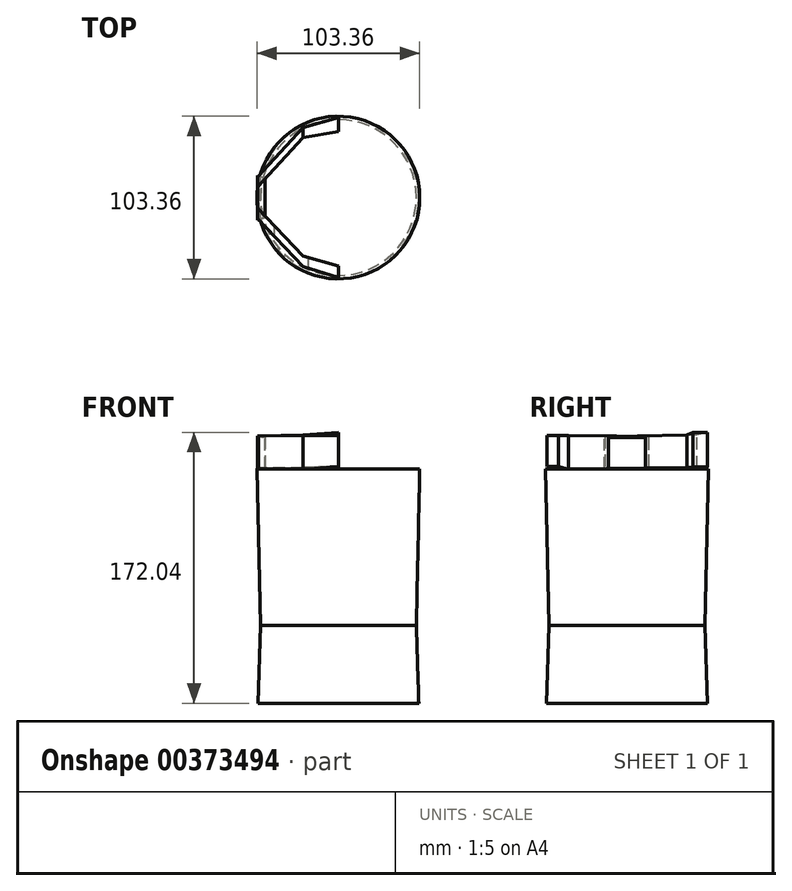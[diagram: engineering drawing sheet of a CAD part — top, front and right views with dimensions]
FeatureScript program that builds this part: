
annotation { "Feature Type Name" : "Feature", "Feature Type Description" : "" }
export const myFeature = defineFeature(function(context is Context, id is Id, definition is map)
    precondition{}
    {
        {
            var Q0;
            Q0=qCreatedBy(makeId("Top.planeOp"),FACE);
            var sketch = newSketch(context, id + "F0", { "sketchPlane" : qUnion([Q0])});
            skCircle(sketch, "E0", {"center": v(0, 0) * mm, "radius": 55.5 * mm});
            skSolve(sketch);
        }
        {
            var Q0;
            Q0=qCreatedBy(makeId("Top.planeOp"),FACE);
            cPlane(context, id + "F1", {"entities" : qUnion([Q0]), "cplaneType" : CPlaneType.OFFSET, "offset" : 25.4 * mm, "width" : 152.4 * mm, "height" : 152.4 * mm});
        }
        {
            var Q0;
            Q0=qCreatedBy(makeId("Top.planeOp"),FACE);
            cPlane(context, id + "F2", {"entities" : qUnion([Q0]), "cplaneType" : CPlaneType.OFFSET, "offset" : 25.91 * mm, "oppositeDirection" : true, "width" : 152.4 * mm, "height" : 152.4 * mm});
        }
        {
            var Q0;
            Q0=qCreatedBy(id+"F2.planeOp",FACE);
            cPlane(context, id + "F3", {"entities" : qUnion([Q0]), "cplaneType" : CPlaneType.OFFSET, "offset" : 76.15 * mm, "width" : 152.4 * mm, "height" : 152.4 * mm});
        }
        {
            var Q0;
            Q0=qCreatedBy(id+"F2.planeOp",FACE);
            cPlane(context, id + "F4", {"entities" : qUnion([Q0]), "cplaneType" : CPlaneType.OFFSET, "offset" : 23.34 * mm, "oppositeDirection" : true, "width" : 152.4 * mm, "height" : 152.4 * mm});
        }
        {
            var Q0;
            Q0=qCreatedBy(id+"F3.planeOp",FACE);
            var sketch = newSketch(context, id + "F5", { "sketchPlane" : qUnion([Q0])});
            skCircle(sketch, "E1", {"center": v(0, 0) * mm, "radius": 54.76 * mm});
            skSolve(sketch);
        }
        {
            var Q0;
            Q0=qCreatedBy(id+"F1.planeOp",FACE);
            var sketch = newSketch(context, id + "F6", { "sketchPlane" : qUnion([Q0])});
            skCircle(sketch, "E2", {"center": v(0, 0) * mm, "radius": 55.5 * mm});
            skSolve(sketch);
        }
        {
            var Q0;
            Q0=qCreatedBy(id+"F2.planeOp",FACE);
            var sketch = newSketch(context, id + "F7", { "sketchPlane" : qUnion([Q0])});
            skCircle(sketch, "E3", {"center": v(0, 0) * mm, "radius": 55.91 * mm});
            skSolve(sketch);
        }
        {
            var Q0;
            Q0=qCreatedBy(id+"F4.planeOp",FACE);
            var sketch = newSketch(context, id + "F8", { "sketchPlane" : qUnion([Q0])});
            skCircle(sketch, "E4", {"center": v(0, 0) * mm, "radius": 55.49 * mm});
            skSolve(sketch);
        }
        {
            var Q0;
            Q0=makeQuery(id+"F8.imprint","IMPRINT",FACE,{"disambiguationData":[TD([[makeQuery(id+"F8.imprint","IMPRINT",EDGE,{"derivedFrom":sQuery(id+"F8.wireOp",EDGE,"E4")}),1.0]])]});
            var sketch = newSketch(context, id + "F9", { "sketchPlane" : qUnion([Q0])});
            skCircle(sketch, "E5", {"center": v(0, 0) * mm, "radius": 49.52 * mm});
            skSolve(sketch);
        }
        {
            var Q0;
            Q0=makeQuery(id+"F5.imprint","IMPRINT",FACE,{"disambiguationData":[TD([[makeQuery(id+"F5.imprint","IMPRINT",EDGE,{"derivedFrom":sQuery(id+"F5.wireOp",EDGE,"E1")}),1.0]])]});
            var sketch = newSketch(context, id + "F10", { "sketchPlane" : qUnion([Q0])});
            skCircle(sketch, "E6", {"center": v(0, 0) * mm, "radius": 51.68 * mm});
            skSolve(sketch);
        }
        {
            var Q0;
            Q0=makeQuery(id+"F10.imprint","IMPRINT",FACE,{"disambiguationData":[TD([[makeQuery(id+"F10.imprint","IMPRINT",EDGE,{"derivedFrom":sQuery(id+"F10.wireOp",EDGE,"E6")}),1.0]])]});
            var Q1;
            Q1=makeQuery(id+"F9.imprint","IMPRINT",FACE,{"disambiguationData":[TD([[makeQuery(id+"F9.imprint","IMPRINT",EDGE,{"derivedFrom":sQuery(id+"F9.wireOp",EDGE,"E5")}),1.0]])]});
            loft(context, id + "F11", {"sheetProfilesArray" : [{ "sheetProfileEntities" : qUnion([Q0]) }, { "sheetProfileEntities" : qUnion([Q1]) }]});
        }
        {
            var Q0;
            Q0=qCreatedBy(id+"F4.planeOp",FACE);
            cPlane(context, id + "F12", {"entities" : qUnion([Q0]), "cplaneType" : CPlaneType.OFFSET, "offset" : 25.01 * mm, "oppositeDirection" : true, "width" : 152.4 * mm, "height" : 152.4 * mm});
        }
        {
            var Q0;
            Q0=qCreatedBy(id+"F12.planeOp",FACE);
            cPlane(context, id + "F13", {"entities" : qUnion([Q0]), "cplaneType" : CPlaneType.OFFSET, "offset" : 24.45 * mm, "oppositeDirection" : true, "width" : 152.4 * mm, "height" : 152.4 * mm});
        }
        {
            var Q0;
            Q0=qCreatedBy(id+"F13.planeOp",FACE);
            var sketch = newSketch(context, id + "F14", { "sketchPlane" : qUnion([Q0])});
            skCircle(sketch, "E7", {"center": v(0, 0) * mm, "radius": 51.1 * mm});
            skSolve(sketch);
        }
        {
            var Q1;
            Q1=makeQuery(id+"F14.imprint","IMPRINT",FACE,{"disambiguationData":[TD([[makeQuery(id+"F14.imprint","IMPRINT",EDGE,{"derivedFrom":sQuery(id+"F14.wireOp",EDGE,"E7")}),1.0]])]});
            var Q2;
            Q2=makeQuery(id+"F11.opLoft","CAP_FACE",FACE,{"disambiguationData":[OSD([makeQuery(id+"F9.imprint","IMPRINT",FACE,{"disambiguationData":[TD([[makeQuery(id+"F9.imprint","IMPRINT",EDGE,{"derivedFrom":sQuery(id+"F9.wireOp",EDGE,"E5")}),1.0]])]})])],"isStart":true});
            loft(context, id + "F15", {"operationType" : NewBodyOperationType.ADD, "sheetProfilesArray" : [{ "sheetProfileEntities" : qUnion([Q1]) }, { "sheetProfileEntities" : qUnion([Q2]) }]});
        }
        {
            var Q0;
            Q0=qCreatedBy(makeId("Right.planeOp"),FACE);
            cPlane(context, id + "F16", {"entities" : qUnion([Q0]), "cplaneType" : CPlaneType.OFFSET, "offset" : 51.44 * mm, "oppositeDirection" : true, "width" : 152.4 * mm, "height" : 152.4 * mm});
        }
        {
            var Q0;
            Q0=qCreatedBy(id+"F16.planeOp",FACE);
            var sketch = newSketch(context, id + "F17", { "sketchPlane" : qUnion([Q0])});
            skLineSegment(sketch, "E8.bottom", {"start": v(-14.21, 50.2) * mm, "end": v(13.86, 50.2) * mm});
            skLineSegment(sketch, "E8.top", {"start": v(-14.21, 70.79) * mm, "end": v(13.86, 70.79) * mm});
            skLineSegment(sketch, "E8.left", {"start": v(-14.21, 50.2) * mm, "end": v(-14.21, 70.79) * mm});
            skLineSegment(sketch, "E8.right", {"start": v(13.86, 50.2) * mm, "end": v(13.86, 70.79) * mm});
            skSolve(sketch);
        }
        {
            var Q0;
            Q0=qCreatedBy(id+"F16.planeOp",FACE);
            cPlane(context, id + "F18", {"entities" : qUnion([Q0]), "cplaneType" : CPlaneType.OFFSET, "offset" : 4.7 * mm, "width" : 152.4 * mm, "height" : 152.4 * mm});
        }
        {
            var Q0;
            Q0=qCreatedBy(makeId("Right.planeOp"),FACE);
            cPlane(context, id + "F19", {"entities" : qUnion([Q0]), "cplaneType" : CPlaneType.OFFSET, "offset" : 22.47 * mm, "oppositeDirection" : true, "width" : 152.4 * mm, "height" : 152.4 * mm});
        }
        {
            var Q0;
            Q0=qCreatedBy(id+"F18.planeOp",FACE);
            var sketch = newSketch(context, id + "F20", { "sketchPlane" : qUnion([Q0])});
            skLineSegment(sketch, "E9.bottom", {"start": v(12.5, 50.3) * mm, "end": v(-12.82, 50.3) * mm});
            skLineSegment(sketch, "E9.top", {"start": v(12.5, 70.21) * mm, "end": v(-12.82, 70.21) * mm});
            skLineSegment(sketch, "E9.left", {"start": v(12.5, 50.3) * mm, "end": v(12.5, 70.21) * mm});
            skLineSegment(sketch, "E9.right", {"start": v(-12.82, 50.3) * mm, "end": v(-12.82, 70.21) * mm});
            skSolve(sketch);
        }
        {
            var Q1;
            Q1=makeQuery(id+"F17.imprint","IMPRINT",FACE,{"disambiguationData":[TD([[makeQuery(id+"F17.imprint","IMPRINT",EDGE,{"derivedFrom":sQuery(id+"F17.wireOp",EDGE,"E8.bottom")}),1.0]])]});
            var Q2;
            Q2=makeQuery(id+"F20.imprint","IMPRINT",FACE,{"disambiguationData":[TD([[makeQuery(id+"F20.imprint","IMPRINT",EDGE,{"derivedFrom":sQuery(id+"F20.wireOp",EDGE,"E9.bottom")}),-1.0]])]});
            loft(context, id + "F21", {"operationType" : NewBodyOperationType.ADD, "sheetProfilesArray" : [{ "sheetProfileEntities" : qUnion([Q1]) }, { "sheetProfileEntities" : qUnion([Q2]) }]});
        }
        {
            var Q0;
            Q0=qCreatedBy(id+"F16.planeOp",FACE);
            var sketch = newSketch(context, id + "F22", { "sketchPlane" : qUnion([Q0])});
            skLineSegment(sketch, "E10.bottom", {"start": v(6.7, 50.6) * mm, "end": v(13.11, 50.6) * mm});
            skLineSegment(sketch, "E10.top", {"start": v(6.7, 71.14) * mm, "end": v(13.11, 71.14) * mm});
            skLineSegment(sketch, "E10.left", {"start": v(6.7, 50.6) * mm, "end": v(6.7, 71.14) * mm});
            skLineSegment(sketch, "E10.right", {"start": v(13.11, 50.6) * mm, "end": v(13.11, 71.14) * mm});
            skLineSegment(sketch, "E11.bottom", {"start": v(-13.4, 50.4) * mm, "end": v(-6.76, 50.4) * mm});
            skLineSegment(sketch, "E11.top", {"start": v(-13.4, 71.15) * mm, "end": v(-6.76, 71.15) * mm});
            skLineSegment(sketch, "E11.left", {"start": v(-13.4, 50.4) * mm, "end": v(-13.4, 71.15) * mm});
            skLineSegment(sketch, "E11.right", {"start": v(-6.76, 50.4) * mm, "end": v(-6.76, 71.15) * mm});
            skSolve(sketch);
        }
        {
            var Q0;
            Q0=qCreatedBy(id+"F19.planeOp",FACE);
            var sketch = newSketch(context, id + "F23", { "sketchPlane" : qUnion([Q0])});
            skLineSegment(sketch, "E12.bottom", {"start": v(44.46, 50.98) * mm, "end": v(38.16, 50.98) * mm});
            skLineSegment(sketch, "E12.top", {"start": v(44.46, 71.79) * mm, "end": v(38.16, 71.79) * mm});
            skLineSegment(sketch, "E12.left", {"start": v(44.46, 50.98) * mm, "end": v(44.46, 71.79) * mm});
            skLineSegment(sketch, "E12.right", {"start": v(38.16, 50.98) * mm, "end": v(38.16, 71.79) * mm});
            skLineSegment(sketch, "E13.bottom", {"start": v(-43.94, 49.96) * mm, "end": v(-37.24, 49.96) * mm});
            skLineSegment(sketch, "E13.top", {"start": v(-43.94, 71.3) * mm, "end": v(-37.24, 71.3) * mm});
            skLineSegment(sketch, "E13.left", {"start": v(-43.94, 49.96) * mm, "end": v(-43.94, 71.3) * mm});
            skLineSegment(sketch, "E13.right", {"start": v(-37.24, 49.96) * mm, "end": v(-37.24, 71.3) * mm});
            skSolve(sketch);
        }
        {
            var Q1;
            Q1=makeQuery(id+"F23.imprint","IMPRINT",FACE,{"disambiguationData":[TD([[makeQuery(id+"F23.imprint","IMPRINT",EDGE,{"derivedFrom":sQuery(id+"F23.wireOp",EDGE,"E12.bottom")}),-1.0]])]});
            var Q2;
            Q2=makeQuery(id+"F22.imprint","IMPRINT",FACE,{"disambiguationData":[TD([[makeQuery(id+"F22.imprint","IMPRINT",EDGE,{"derivedFrom":sQuery(id+"F22.wireOp",EDGE,"E10.bottom")}),1.0]])]});
            loft(context, id + "F24", {"operationType" : NewBodyOperationType.ADD, "sheetProfilesArray" : [{ "sheetProfileEntities" : qUnion([Q1]) }, { "sheetProfileEntities" : qUnion([Q2]) }]});
        }
        {
            var Q1;
            Q1=makeQuery(id+"F22.imprint","IMPRINT",FACE,{"disambiguationData":[TD([[makeQuery(id+"F22.imprint","IMPRINT",EDGE,{"derivedFrom":sQuery(id+"F22.wireOp",EDGE,"E11.bottom")}),1.0]])]});
            var Q2;
            Q2=makeQuery(id+"F23.imprint","IMPRINT",FACE,{"disambiguationData":[TD([[makeQuery(id+"F23.imprint","IMPRINT",EDGE,{"derivedFrom":sQuery(id+"F23.wireOp",EDGE,"E13.bottom")}),1.0]])]});
            loft(context, id + "F25", {"operationType" : NewBodyOperationType.ADD, "sheetProfilesArray" : [{ "sheetProfileEntities" : qUnion([Q1]) }, { "sheetProfileEntities" : qUnion([Q2]) }]});
        }
        {
            var Q0;
            Q0=qCreatedBy(makeId("Right.planeOp"),FACE);
            var sketch = newSketch(context, id + "F26", { "sketchPlane" : qUnion([Q0])});
            skLineSegment(sketch, "E14.bottom", {"start": v(-50.84, 51.86) * mm, "end": v(-43.54, 51.86) * mm});
            skLineSegment(sketch, "E14.top", {"start": v(-50.84, 71.39) * mm, "end": v(-43.54, 71.39) * mm});
            skLineSegment(sketch, "E14.left", {"start": v(-50.84, 51.86) * mm, "end": v(-50.84, 71.39) * mm});
            skLineSegment(sketch, "E14.right", {"start": v(-43.54, 51.86) * mm, "end": v(-43.54, 71.39) * mm});
            skSolve(sketch);
        }
        {
            var Q1;
            Q1=makeQuery(id+"F23.imprint","IMPRINT",FACE,{"disambiguationData":[TD([[makeQuery(id+"F23.imprint","IMPRINT",EDGE,{"derivedFrom":sQuery(id+"F23.wireOp",EDGE,"E13.bottom")}),1.0]])]});
            var Q2;
            Q2=makeQuery(id+"F26.imprint","IMPRINT",FACE,{"disambiguationData":[TD([[makeQuery(id+"F26.imprint","IMPRINT",EDGE,{"derivedFrom":sQuery(id+"F26.wireOp",EDGE,"E14.bottom")}),1.0]])]});
            loft(context, id + "F27", {"operationType" : NewBodyOperationType.ADD, "sheetProfilesArray" : [{ "sheetProfileEntities" : qUnion([Q1]) }, { "sheetProfileEntities" : qUnion([Q2]) }]});
        }
        {
            var Q0;
            Q0=qCreatedBy(makeId("Right.planeOp"),FACE);
            var sketch = newSketch(context, id + "F28", { "sketchPlane" : qUnion([Q0])});
            skLineSegment(sketch, "E15.bottom", {"start": v(50.94, 51.55) * mm, "end": v(41.88, 51.55) * mm});
            skLineSegment(sketch, "E15.top", {"start": v(50.94, 73.33) * mm, "end": v(41.88, 73.33) * mm});
            skLineSegment(sketch, "E15.left", {"start": v(50.94, 51.55) * mm, "end": v(50.94, 73.33) * mm});
            skLineSegment(sketch, "E15.right", {"start": v(41.88, 51.55) * mm, "end": v(41.88, 73.33) * mm});
            skSolve(sketch);
        }
        {
            var Q1;
            Q1=makeQuery(id+"F28.imprint","IMPRINT",FACE,{"disambiguationData":[TD([[makeQuery(id+"F28.imprint","IMPRINT",EDGE,{"derivedFrom":sQuery(id+"F28.wireOp",EDGE,"E15.bottom")}),-1.0]])]});
            var Q2;
            Q2=makeQuery(id+"F23.imprint","IMPRINT",FACE,{"disambiguationData":[TD([[makeQuery(id+"F23.imprint","IMPRINT",EDGE,{"derivedFrom":sQuery(id+"F23.wireOp",EDGE,"E12.bottom")}),-1.0]])]});
            loft(context, id + "F29", {"operationType" : NewBodyOperationType.ADD, "sheetProfilesArray" : [{ "sheetProfileEntities" : qUnion([Q1]) }, { "sheetProfileEntities" : qUnion([Q2]) }]});
        }
    });
